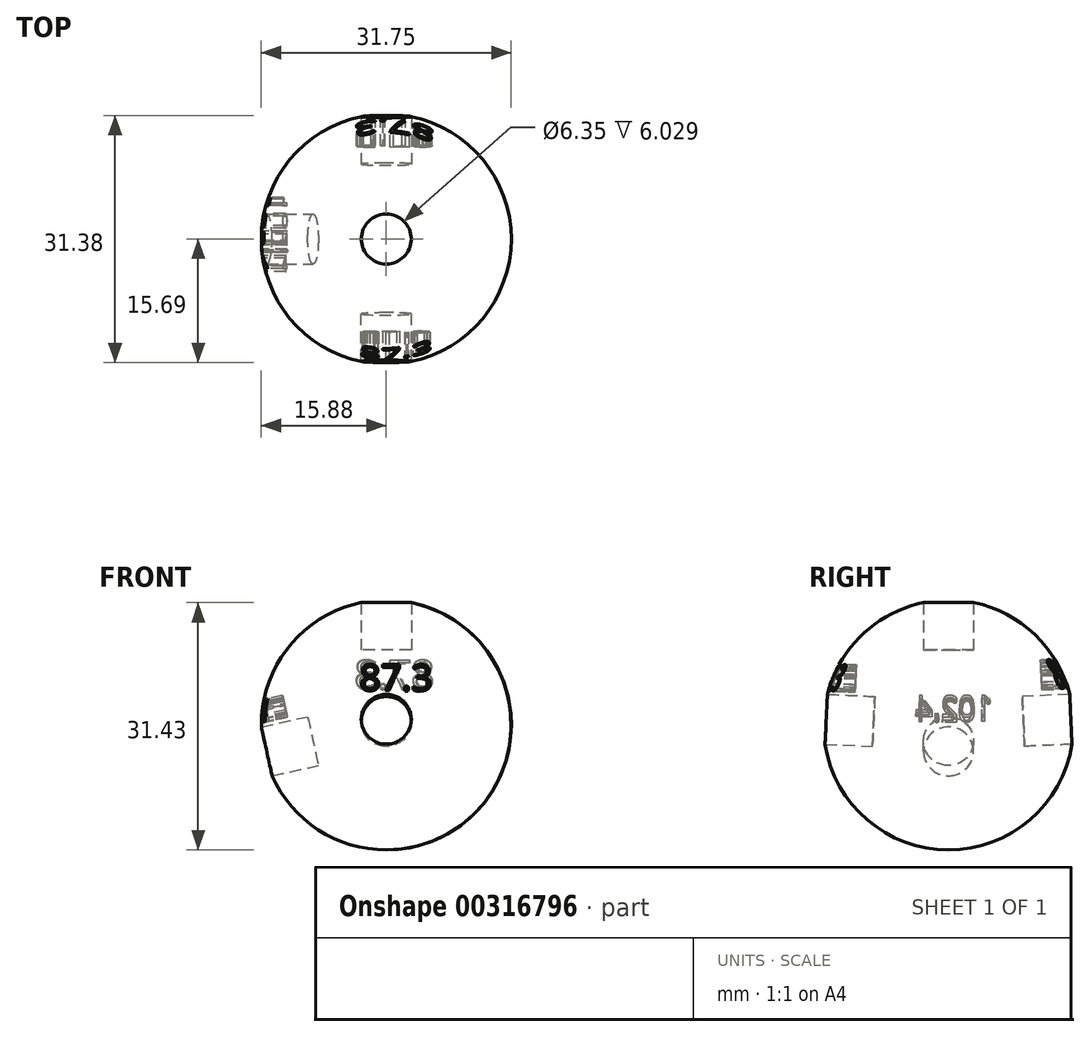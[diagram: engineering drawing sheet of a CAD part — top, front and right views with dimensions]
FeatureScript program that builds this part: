
annotation { "Feature Type Name" : "Feature", "Feature Type Description" : "" }
export const myFeature = defineFeature(function(context is Context, id is Id, definition is map)
    precondition{}
    {
        {
            var Q0;
            Q0=qCreatedBy(makeId("Front.planeOp"),FACE);
            var sketch = newSketch(context, id + "F0", { "sketchPlane" : qUnion([Q0])});
            skArc(sketch, "E0", {"start": v(0, 15.88) * mm, "mid": v(-15.88, 0) * mm, "end": v(0, -15.88) * mm});
            skLineSegment(sketch, "E1", {"start": v(0, 15.88) * mm, "end": v(0, -15.88) * mm});
            skSolve(sketch);
        }
        {
            var Q0;
            Q0=qCreatedBy(makeId("Top.planeOp"),FACE);
            var sketch = newSketch(context, id + "F1", { "sketchPlane" : qUnion([Q0])});
            skCircle(sketch, "E2", {"center": v(0, 0) * mm, "radius": 15.88 * mm});
            skSolve(sketch);
        }
        {
            var Q0;
            Q0=makeQuery(id+"F0.imprint","IMPRINT",FACE,{"disambiguationData":[TD([[makeQuery(id+"F0.imprint","IMPRINT",EDGE,{"derivedFrom":sQuery(id+"F0.wireOp",EDGE,"E0")}),1.0]])]});
            var Q1;
            Q1=sQuery(id+"F1.wireOp",EDGE,"E2");
            revolve(context, id + "F2", {"entities" : qUnion([Q0]), "axis" : qUnion([Q1]), "revolveType" : RevolveType.FULL});
        }
        {
            var Q0;
            Q0=qCreatedBy(makeId("Front.planeOp"),FACE);
            var sketch = newSketch(context, id + "F3", { "sketchPlane" : qUnion([Q0])});
            skLineSegment(sketch, "E3", {"start": v(-30.42, 0) * mm, "end": v(37.24, 0) * mm});
            skLineSegment(sketch, "E4", {"start": v(0, 33.55) * mm, "end": v(0, -37.42) * mm});
            skSolve(sketch);
        }
        {
            var Q0;
            Q0=qCreatedBy(makeId("Top.planeOp"),FACE);
            var sketch = newSketch(context, id + "F4", { "sketchPlane" : qUnion([Q0])});
            skLineSegment(sketch, "E5", {"start": v(0, 33.18) * mm, "end": v(0, -39.45) * mm});
            skSolve(sketch);
        }
        {
            var Q0;
            Q0=qCreatedBy(makeId("Top.planeOp"),FACE);
            cPlane(context, id + "F5", {"entities" : qUnion([Q0]), "cplaneType" : CPlaneType.OFFSET, "offset" : 9.52 * mm, "width" : 152.4 * mm, "height" : 152.4 * mm});
        }
        {
            var Q0;
            Q0=qCreatedBy(id+"F5.planeOp",FACE);
            var sketch = newSketch(context, id + "F6", { "sketchPlane" : qUnion([Q0])});
            skCircle(sketch, "E6", {"center": v(0, 0) * mm, "radius": 3.18 * mm});
            skSolve(sketch);
        }
        {
            var Q0;
            Q0 = qSketchRegion(id + "F6", true);
            extrude(context, id + "F7", {"entities" : qUnion([Q0]), "depth" : 50.8 * mm});
        }
        {
            var Q0;
            Q0=makeQuery(id+"F7.opExtrude","SWEPT_BODY",BODY,{"disambiguationData":[OSD([sQuery(id+"F6.wireOp",EDGE,"E6")])]});
            var Q1;
            Q1=sQuery(id+"F3.wireOp",EDGE,"E3");
            transform(context, id + "F8", {"entities" : qUnion([Q0]), "transformType" : TransformType.ROTATION, "transformAxis" : qUnion([Q1]), "angle" : 87.3 * degree, "makeCopy" : true});
        }
        {
            var Q0;
            Q0=makeQuery(id+"F7.opExtrude","SWEPT_BODY",BODY,{"disambiguationData":[OSD([sQuery(id+"F6.wireOp",EDGE,"E6")])]});
            var Q1;
            Q1=sQuery(id+"F4.wireOp",EDGE,"E5");
            transform(context, id + "F9", {"entities" : qUnion([Q0]), "transformType" : TransformType.ROTATION, "transformAxis" : qUnion([Q1]), "angle" : 102.4 * degree, "makeCopy" : true});
        }
        {
            var Q0;
            Q0=qCreatedBy(makeId("Front.planeOp"),FACE);
            var sketch = newSketch(context, id + "F10", { "sketchPlane" : qUnion([Q0])});
            skLineSegment(sketch, "E7", {"start": v(61.4, 0) * mm, "end": v(-77.88, 0) * mm});
            skSolve(sketch);
        }
        {
            var Q0;
            Q0=makeQuery(id+"F7.opExtrude","SWEPT_BODY",BODY,{"disambiguationData":[OSD([sQuery(id+"F6.wireOp",EDGE,"E6")])]});
            var Q1;
            Q1=sQuery(id+"F10.wireOp",EDGE,"E7");
            transform(context, id + "F11", {"entities" : qUnion([Q0]), "transformType" : TransformType.ROTATION, "transformAxis" : qUnion([Q1]), "angle" : 87.3 * degree, "makeCopy" : true});
        }
        {
            var Q0;
            Q0=makeQuery(id+"F11.opPattern","COPY",FACE,{"derivedFrom":makeQuery(id+"F7.opExtrude","CAP_FACE",FACE,{"disambiguationData":[OSD([sQuery(id+"F6.wireOp",EDGE,"E6")])],"isStart":false}),"instanceName":"1"});
            cPlane(context, id + "F12", {"entities" : qUnion([Q0]), "cplaneType" : CPlaneType.OFFSET, "offset" : 44.45 * mm, "oppositeDirection" : true, "width" : 152.4 * mm, "height" : 152.4 * mm});
        }
        {
            var Q0;
            Q0=qCreatedBy(id+"F12.planeOp",FACE);
            var sketch = newSketch(context, id + "F13", { "sketchPlane" : qUnion([Q0])});
            skText(sketch, "E8", { "text": "87.3", "fontName": "OpenSans-Regular.ttf"});
            const initialGuessF13  = {"E8": [-0.0061, 0.00398, 1, 0, 0.0037]};
            skSetInitialGuess(sketch, initialGuessF13);
            skSolve(sketch);
        }
        {
            var Q0;
            Q0 = qSketchRegion(id + "F13", true);
            extrude(context, id + "F14", {"entities" : qUnion([Q0]), "operationType" : NewBodyOperationType.REMOVE, "oppositeDirection" : true, "depth" : 3.8 * mm});
        }
        {
            var Q0;
            Q0=makeQuery(id+"F9.opPattern","COPY",FACE,{"derivedFrom":makeQuery(id+"F7.opExtrude","CAP_FACE",FACE,{"disambiguationData":[OSD([sQuery(id+"F6.wireOp",EDGE,"E6")])],"isStart":false}),"instanceName":"1"});
            cPlane(context, id + "F15", {"entities" : qUnion([Q0]), "cplaneType" : CPlaneType.OFFSET, "offset" : 44.45 * mm, "oppositeDirection" : true, "width" : 152.4 * mm, "height" : 152.4 * mm});
        }
        {
            var Q0;
            Q0=makeQuery(id+"F8.opPattern","COPY",FACE,{"derivedFrom":makeQuery(id+"F7.opExtrude","CAP_FACE",FACE,{"disambiguationData":[OSD([sQuery(id+"F6.wireOp",EDGE,"E6")])],"isStart":false}),"instanceName":"1"});
            cPlane(context, id + "F16", {"entities" : qUnion([Q0]), "cplaneType" : CPlaneType.OFFSET, "offset" : 44.45 * mm, "oppositeDirection" : true, "width" : 152.4 * mm, "height" : 152.4 * mm});
        }
        {
            var Q0;
            Q0=qCreatedBy(id+"F16.planeOp",FACE);
            var sketch = newSketch(context, id + "F17", { "sketchPlane" : qUnion([Q0])});
            skText(sketch, "E9", { "text": "87.3", "fontName": "OpenSans-Regular.ttf"});
            const initialGuessF17  = {"E9": [-0.00339, 0.00368, 1, 0, 0.00336]};
            skSetInitialGuess(sketch, initialGuessF17);
            skSolve(sketch);
        }
        {
            var Q0;
            Q0 = qSketchRegion(id + "F17", true);
            extrude(context, id + "F18", {"entities" : qUnion([Q0]), "operationType" : NewBodyOperationType.REMOVE, "oppositeDirection" : true, "depth" : 3.8 * mm});
        }
        {
            var Q0;
            Q0=makeQuery(id+"F7.opExtrude","SWEPT_BODY",BODY,{"disambiguationData":[OSD([sQuery(id+"F6.wireOp",EDGE,"E6")])]});
            var Q1;
            Q1=makeQuery(id+"F8.opPattern","COPY",BODY,{"derivedFrom":makeQuery(id+"F7.opExtrude","SWEPT_BODY",BODY,{"disambiguationData":[OSD([sQuery(id+"F6.wireOp",EDGE,"E6")])]}),"instanceName":"1"});
            var Q2;
            Q2=makeQuery(id+"F11.opPattern","COPY",BODY,{"derivedFrom":makeQuery(id+"F7.opExtrude","SWEPT_BODY",BODY,{"disambiguationData":[OSD([sQuery(id+"F6.wireOp",EDGE,"E6")])]}),"instanceName":"1"});
            var Q3;
            Q3=makeQuery(id+"F9.opPattern","COPY",BODY,{"derivedFrom":makeQuery(id+"F7.opExtrude","SWEPT_BODY",BODY,{"disambiguationData":[OSD([sQuery(id+"F6.wireOp",EDGE,"E6")])]}),"instanceName":"1"});
            var Q4;
            Q4=makeQuery(id+"F2.opRevolve","SWEPT_BODY",BODY,{"disambiguationData":[OSD([sQuery(id+"F0.wireOp",EDGE,"E0"),sQuery(id+"F0.wireOp",EDGE,"E1")])]});
            booleanBodies(context, id + "F19", {"operationType" : BooleanOperationType.SUBTRACTION, "tools" : qUnion([Q0, Q1, Q2, Q3]), "targets" : qUnion([Q4])});
        }
        {
            var Q0;
            Q0=qCreatedBy(id+"F15.planeOp",FACE);
            var sketch = newSketch(context, id + "F20", { "sketchPlane" : qUnion([Q0])});
            skText(sketch, "E10", { "text": "102.4", "fontName": "OpenSans-Regular.ttf"});
            const initialGuessF20  = {"E10": [-0.00561, 0.00373, 1, 0, 0.00277]};
            skSetInitialGuess(sketch, initialGuessF20);
            skSolve(sketch);
        }
        {
            var Q0;
            Q0 = qSketchRegion(id + "F20", true);
            extrude(context, id + "F21", {"entities" : qUnion([Q0]), "operationType" : NewBodyOperationType.REMOVE, "oppositeDirection" : true, "depth" : 3.8 * mm});
        }
    });
